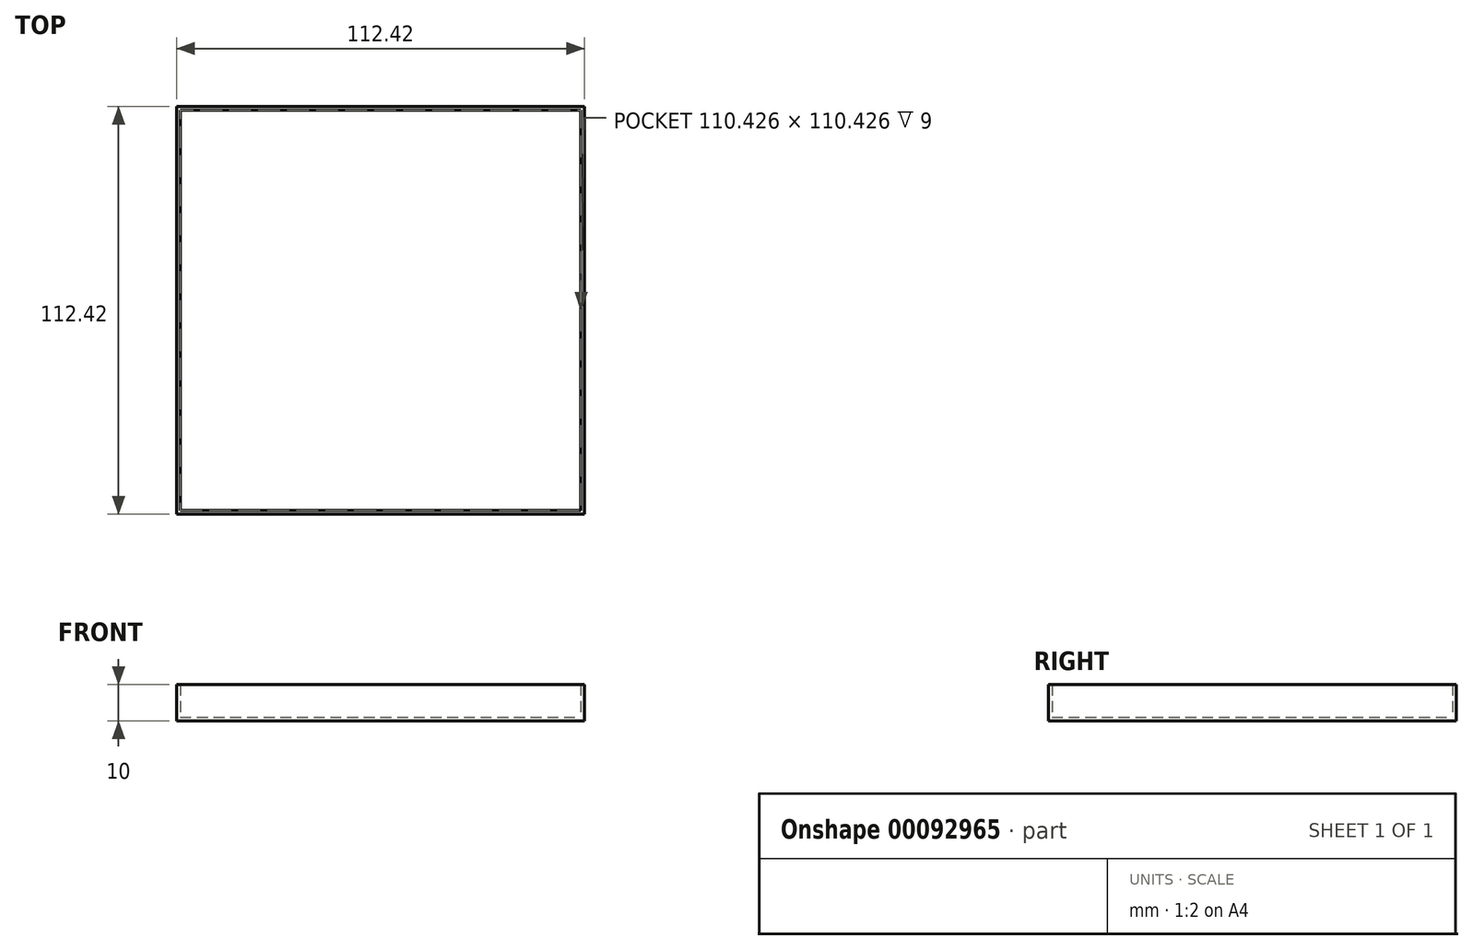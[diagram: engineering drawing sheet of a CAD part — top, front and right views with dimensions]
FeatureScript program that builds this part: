
annotation { "Feature Type Name" : "Feature", "Feature Type Description" : "" }
export const myFeature = defineFeature(function(context is Context, id is Id, definition is map)
    precondition{}
    {
        {
            var Q0;
            Q0=qCreatedBy(makeId("Top.planeOp"),FACE);
            var sketch = newSketch(context, id + "F0", { "sketchPlane" : qUnion([Q0])});
            skCircle(sketch, "E0.cCircle", {"center": v(0, 0) * mm, "radius": 56.21 * mm, "construction": true});
            skLineSegment(sketch, "E0.0", {"start": v(-56.21, 56.21) * mm, "end": v(56.21, 56.21) * mm});
            skLineSegment(sketch, "E0.1", {"start": v(56.21, 56.21) * mm, "end": v(56.21, -56.21) * mm});
            skLineSegment(sketch, "E0.2", {"start": v(56.21, -56.21) * mm, "end": v(-56.21, -56.21) * mm});
            skLineSegment(sketch, "E0.3", {"start": v(-56.21, -56.21) * mm, "end": v(-56.21, 56.21) * mm});
            skPoint(sketch, "E0.0.midPoint", {"position": v(0, 56.21) * mm});
            skSolve(sketch);
        }
        {
            var Q0;
            Q0 = qSketchRegion(id + "F0", true);
            extrude(context, id + "F1", {"entities" : qUnion([Q0]), "depth" : 10 * mm});
        }
        {
            var Q0;
            Q0=makeQuery(id+"F1.opExtrude","CAP_FACE",FACE,{"disambiguationData":[OSD([sQuery(id+"F0.wireOp",EDGE,"E0.0"),sQuery(id+"F0.wireOp",EDGE,"E0.1"),sQuery(id+"F0.wireOp",EDGE,"E0.2"),sQuery(id+"F0.wireOp",EDGE,"E0.3")])],"isStart":false});
            shell(context, id + "F2", {"entities" : qUnion([Q0]), "thickness" : 1 * mm});
        }
    });
